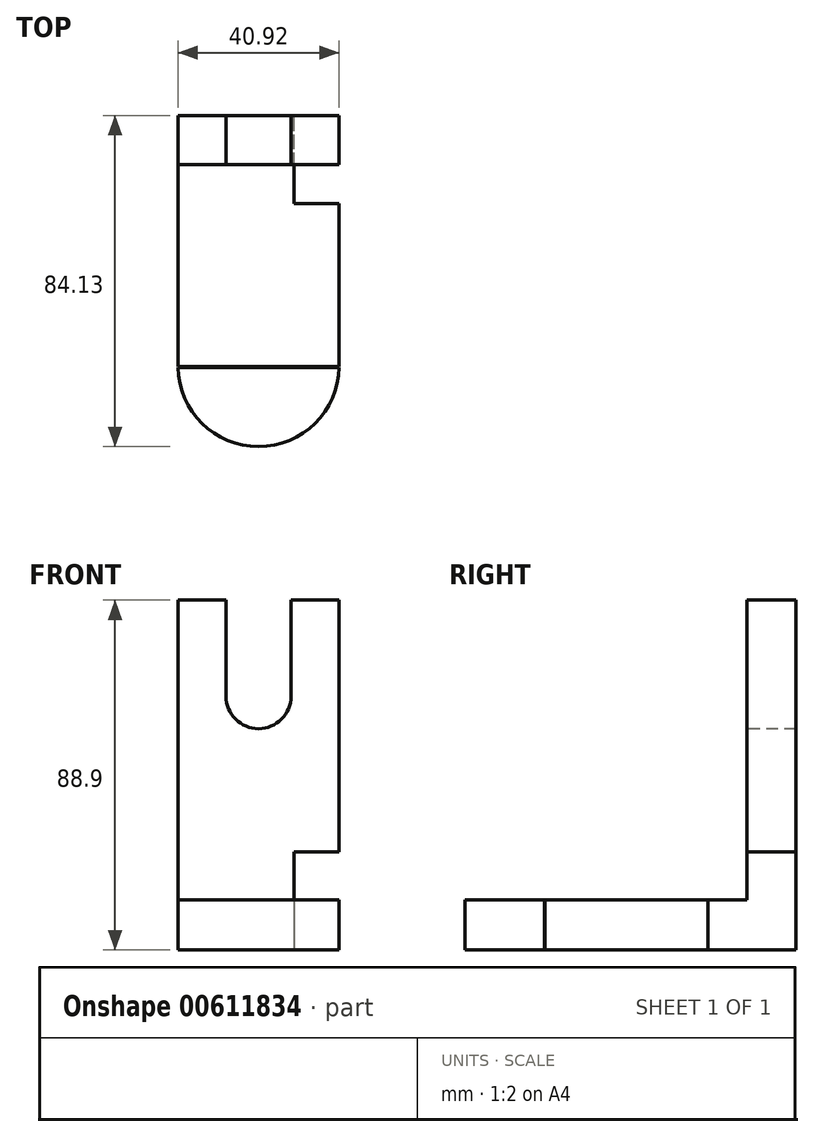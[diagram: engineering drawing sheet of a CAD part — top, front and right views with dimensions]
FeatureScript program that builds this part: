
annotation { "Feature Type Name" : "Feature", "Feature Type Description" : "" }
export const myFeature = defineFeature(function(context is Context, id is Id, definition is map)
    precondition{}
    {
        {
            var Q0;
            Q0=qCreatedBy(makeId("Top.planeOp"),FACE);
            var sketch = newSketch(context, id + "F0", { "sketchPlane" : qUnion([Q0])});
            skLineSegment(sketch, "E0.bottom", {"start": v(-20.46, -31.89) * mm, "end": v(20.46, -31.89) * mm});
            skLineSegment(sketch, "E0.top", {"start": v(-20.46, 31.89) * mm, "end": v(20.46, 31.89) * mm});
            skLineSegment(sketch, "E0.left", {"start": v(-20.46, -31.89) * mm, "end": v(-20.46, 31.89) * mm});
            skLineSegment(sketch, "E0.right", {"start": v(20.46, -31.89) * mm, "end": v(20.46, 31.89) * mm});
            skPoint(sketch, "E0.middle", {"position": v(0, 0) * mm});
            skSolve(sketch);
        }
        {
            var Q0;
            Q0=makeQuery(id+"F0.imprint","IMPRINT",FACE,{"disambiguationData":[TD([[makeQuery(id+"F0.imprint","IMPRINT",EDGE,{"derivedFrom":sQuery(id+"F0.wireOp",EDGE,"E0.bottom")}),1.0]])]});
            var sketch = newSketch(context, id + "F1", { "sketchPlane" : qUnion([Q0])});
            skArc(sketch, "E1", {"start": v(-20.43, -32.1) * mm, "mid": v(0, -52.24) * mm, "end": v(20.43, -32.1) * mm});
            skLineSegment(sketch, "E2", {"start": v(-20.43, -32.1) * mm, "end": v(20.43, -32.1) * mm});
            skSolve(sketch);
        }
        {
            var Q0;
            Q0 = qSketchRegion(id + "F0", true);
            var Q1;
            Q1=makeQuery(id+"F1.imprint","IMPRINT",FACE,{"disambiguationData":[TD([[makeQuery(id+"F1.imprint","IMPRINT",EDGE,{"derivedFrom":sQuery(id+"F1.wireOp",EDGE,"E1")}),1.0]])]});
            extrude(context, id + "F2", {"entities" : qUnion([Q0, Q1]), "depth" : 12.7 * mm, "offsetDistance" : 25.4 * mm});
        }
        {
            var Q0;
            Q0=makeQuery(id+"F2.opExtrude","CAP_FACE",FACE,{"disambiguationData":[OSD([sQuery(id+"F0.wireOp",EDGE,"E0.bottom"),sQuery(id+"F0.wireOp",EDGE,"E0.top"),sQuery(id+"F0.wireOp",EDGE,"E0.left"),sQuery(id+"F0.wireOp",EDGE,"E0.right")])],"isStart":false});
            var sketch = newSketch(context, id + "F3", { "sketchPlane" : qUnion([Q0])});
            skLineSegment(sketch, "E3.bottom", {"start": v(-20.46, 31.89) * mm, "end": v(20.46, 31.89) * mm});
            skLineSegment(sketch, "E3.top", {"start": v(-20.46, 19.43) * mm, "end": v(20.46, 19.43) * mm});
            skLineSegment(sketch, "E3.left", {"start": v(-20.46, 31.89) * mm, "end": v(-20.46, 19.43) * mm});
            skLineSegment(sketch, "E3.right", {"start": v(20.46, 31.89) * mm, "end": v(20.46, 19.43) * mm});
            skSolve(sketch);
        }
        {
            var Q0;
            Q0 = qSketchRegion(id + "F3", true);
            extrude(context, id + "F4", {"entities" : qUnion([Q0]), "operationType" : NewBodyOperationType.ADD, "depth" : 76.2 * mm, "offsetDistance" : 25.4 * mm});
        }
        {
            var Q0;
            Q0=makeQuery(id+"F4.opExtrude","SWEPT_FACE",FACE,{"disambiguationData":[OSD([sQuery(id+"F3.wireOp",EDGE,"E3.top")])]});
            var sketch = newSketch(context, id + "F5", { "sketchPlane" : qUnion([Q0])});
            skLineSegment(sketch, "E4.bottom", {"start": v(-8.26, 88.9) * mm, "end": v(8.26, 88.9) * mm});
            skLineSegment(sketch, "E4.left", {"start": v(-8.26, 88.9) * mm, "end": v(-8.26, 64.5) * mm});
            skLineSegment(sketch, "E4.right", {"start": v(8.26, 88.9) * mm, "end": v(8.26, 64.5) * mm});
            skArc(sketch, "E5", {"start": v(-8.26, 64.5) * mm, "mid": v(0, 56.24) * mm, "end": v(8.26, 64.5) * mm});
            skSolve(sketch);
        }
        {
            var Q0;
            Q0=makeQuery(id+"F5.imprint","IMPRINT",FACE,{"disambiguationData":[TD([[makeQuery(id+"F5.imprint","IMPRINT",EDGE,{"derivedFrom":sQuery(id+"F5.wireOp",EDGE,"E4.bottom")}),-1.0]])]});
            extrude(context, id + "F6", {"entities" : qUnion([Q0]), "operationType" : NewBodyOperationType.REMOVE, "oppositeDirection" : true, "depth" : 25.4 * mm, "offsetDistance" : 25.4 * mm});
        }
        {
            var Q0;
            Q0=makeQuery(id+"F4.boolean.opBoolean","MERGE",FACE,{"derivedFrom":[makeQuery(id+"F2.opExtrude","SWEPT_FACE",FACE,{"disambiguationData":[OSD([sQuery(id+"F0.wireOp",EDGE,"E0.right")])]}),makeQuery(id+"F4.opExtrude","SWEPT_FACE",FACE,{"disambiguationData":[OSD([sQuery(id+"F3.wireOp",EDGE,"E3.right")])]})]});
            var sketch = newSketch(context, id + "F7", { "sketchPlane" : qUnion([Q0])});
            skLineSegment(sketch, "E6.bottom", {"start": v(9.5, 17.42) * mm, "end": v(19.43, 17.42) * mm});
            skLineSegment(sketch, "E6.top", {"start": v(9.5, 0) * mm, "end": v(40.69, 0) * mm});
            skLineSegment(sketch, "E6.left", {"start": v(9.5, 17.42) * mm, "end": v(9.5, 0) * mm});
            skLineSegment(sketch, "E6.right", {"start": v(40.69, 17.42) * mm, "end": v(40.69, 0) * mm});
            skPoint(sketch, "E7.firstSnap0", {"position": v(19.43, 50.8) * mm});
            skLineSegment(sketch, "E7.top", {"start": v(19.43, 24.9) * mm, "end": v(31.89, 24.9) * mm});
            skLineSegment(sketch, "E7.left", {"start": v(19.43, 17.42) * mm, "end": v(19.43, 24.9) * mm});
            skLineSegment(sketch, "E7.right", {"start": v(31.89, 17.42) * mm, "end": v(31.89, 24.9) * mm});
            skLineSegment(sketch, "E8.trimOffspring", {"start": v(31.89, 17.42) * mm, "end": v(40.69, 17.42) * mm});
            skSolve(sketch);
        }
        {
            var Q0;
            Q0=makeQuery(id+"F7.imprint","IMPRINT",FACE,{"disambiguationData":[TD([[makeQuery(id+"F7.imprint","IMPRINT",EDGE,{"derivedFrom":sQuery(id+"F7.wireOp",EDGE,"E7.top")}),-1.0]])]});
            var Q1;
            {var subQ3=sQuery(id+"F7.wireOp",EDGE,"E6.right");Q1=makeQuery(id+"F7.imprint","IMPRINT",FACE,{"disambiguationData":[TD([[makeQuery(id+"F7.imprint","IMPRINT",EDGE,{"derivedFrom":subQ3}),-1.0]])]});}
            extrude(context, id + "F8", {"entities" : qUnion([Q0, Q1]), "operationType" : NewBodyOperationType.REMOVE, "oppositeDirection" : true, "depth" : 11.43 * mm, "offsetDistance" : 25.4 * mm});
        }
    });
